annotation { "Feature Type Name" : "Feature", "Feature Type Description" : "" }
export const myFeature = defineFeature(function(context is Context, id is Id, definition is map)
    precondition{}
    {
        {
            var Q0;
            Q0=qCreatedBy(makeId("Front.planeOp"),FACE);
            var sketch = newSketch(context, id + "F0", { "sketchPlane" : qUnion([Q0])});
            skLineSegment(sketch, "E0.bottom", {"start": v(65, 37.5) * mm, "end": v(-65, 37.5) * mm});
            skLineSegment(sketch, "E0.top", {"start": v(65, -37.5) * mm, "end": v(-65, -37.5) * mm});
            skLineSegment(sketch, "E0.left", {"start": v(65, 37.5) * mm, "end": v(65, -37.5) * mm});
            skLineSegment(sketch, "E0.right", {"start": v(-65, 37.5) * mm, "end": v(-65, -37.5) * mm});
            skPoint(sketch, "E0.middle", {"position": v(0, 0) * mm});
            skSolve(sketch);
        }
        {
            var Q0;
            Q0 = qSketchRegion(id + "F0", true);
            extrude(context, id + "F1", {"entities" : qUnion([Q0]), "depth" : .6 * mm, "offsetDistance" : 25 * mm});
        }
        {
            var Q0;
            Q0=makeQuery(id+"F1.opExtrude","CAP_FACE",FACE,{"disambiguationData":[OSD([sQuery(id+"F0.wireOp",EDGE,"E0.bottom"),sQuery(id+"F0.wireOp",EDGE,"E0.top"),sQuery(id+"F0.wireOp",EDGE,"E0.left"),sQuery(id+"F0.wireOp",EDGE,"E0.right")])],"isStart":false});
            var sketch = newSketch(context, id + "F2", { "sketchPlane" : qUnion([Q0])});
            skText(sketch, "E1", { "text": "Prescription:", "fontName": "Tinos-Bold.ttf"});
            const initialGuessF2  = {"E1": [-0.064, 0.0285, 1, 0, 0.008]};
            skSetInitialGuess(sketch, initialGuessF2);
            skSolve(sketch);
        }
        {
            var Q0;
            Q0 = qSketchRegion(id + "F2", true);
            extrude(context, id + "F3", {"entities" : qUnion([Q0]), "operationType" : NewBodyOperationType.ADD, "depth" : .8 * mm, "offsetDistance" : 25 * mm});
        }
        {
            var Q0;
            {var subQ0=sQuery(id+"F0.wireOp",EDGE,"E0.bottom");var subQ1=sQuery(id+"F0.wireOp",EDGE,"E0.right");var subQ2=sQuery(id+"F0.wireOp",EDGE,"E0.top");var subQ3=sQuery(id+"F0.wireOp",EDGE,"E0.left");Q0=makeQuery(id+"F3.boolean.opBoolean","SPLIT",FACE,{"disambiguationData":[TD([makeQuery(id+"F1.opExtrude","SWEPT_FACE",FACE,{"disambiguationData":[OSD([subQ0])]})])],"derivedFrom":makeQuery(id+"F1.opExtrude","CAP_FACE",FACE,{"disambiguationData":[OSD([subQ0,subQ2,subQ3,subQ1])],"isStart":false})});}
            var sketch = newSketch(context, id + "F4", { "sketchPlane" : qUnion([Q0])});
            skText(sketch, "E2", { "text": "Beer", "fontName": "Tinos-Bold.ttf"});
            const initialGuessF4  = {"E2": [0.003, 0.0245, 1, 0, 0.01]};
            skSetInitialGuess(sketch, initialGuessF4);
            skSolve(sketch);
        }
        {
            var Q0;
            Q0 = qSketchRegion(id + "F4", true);
            extrude(context, id + "F5", {"entities" : qUnion([Q0]), "operationType" : NewBodyOperationType.ADD, "depth" : .8 * mm, "offsetDistance" : 25 * mm});
        }
        {
            var Q0;
            {var subQ118=sQuery(id+"F0.wireOp",EDGE,"E0.bottom");var subQ119=makeQuery(id+"F1.opExtrude","SWEPT_FACE",FACE,{"disambiguationData":[OSD([subQ118])]});var subQ124=sQuery(id+"F0.wireOp",EDGE,"E0.right");var subQ130=sQuery(id+"F0.wireOp",EDGE,"E0.top");var subQ139=sQuery(id+"F0.wireOp",EDGE,"E0.left");Q0=makeQuery(id+"F5.boolean.opBoolean","SPLIT",FACE,{"disambiguationData":[TD([subQ119])],"derivedFrom":makeQuery(id+"F3.boolean.opBoolean","SPLIT",FACE,{"disambiguationData":[TD([subQ119])],"derivedFrom":makeQuery(id+"F1.opExtrude","CAP_FACE",FACE,{"disambiguationData":[OSD([subQ118,subQ130,subQ139,subQ124])],"isStart":false})})});}
            var sketch = newSketch(context, id + "F6", { "sketchPlane" : qUnion([Q0])});
            skLineSegment(sketch, "E3.bottom", {"start": v(-65, 22.5) * mm, "end": v(65, 22.5) * mm});
            skLineSegment(sketch, "E3.top", {"start": v(-65, 21.5) * mm, "end": v(65, 21.5) * mm});
            skLineSegment(sketch, "E3.left", {"start": v(-65, 22.5) * mm, "end": v(-65, 21.5) * mm});
            skLineSegment(sketch, "E3.right", {"start": v(65, 22.5) * mm, "end": v(65, 21.5) * mm});
            skSolve(sketch);
        }
        {
            var Q0;
            Q0 = qSketchRegion(id + "F6", true);
            extrude(context, id + "F7", {"entities" : qUnion([Q0]), "operationType" : NewBodyOperationType.ADD, "depth" : .8 * mm, "offsetDistance" : 25 * mm});
        }
        {
            var Q0;
            {var subQ0=sQuery(id+"F0.wireOp",EDGE,"E0.right");var subQ2=sQuery(id+"F0.wireOp",EDGE,"E0.top");var subQ3=makeQuery(id+"F1.opExtrude","SWEPT_FACE",FACE,{"disambiguationData":[OSD([subQ2])]});var subQ4=sQuery(id+"F0.wireOp",EDGE,"E0.left");var subQ124=sQuery(id+"F0.wireOp",EDGE,"E0.bottom");var subQ125=makeQuery(id+"F1.opExtrude","SWEPT_FACE",FACE,{"disambiguationData":[OSD([subQ124])]});Q0=makeQuery(id+"F7.boolean.opBoolean","SPLIT",FACE,{"disambiguationData":[TD([subQ3])],"derivedFrom":makeQuery(id+"F5.boolean.opBoolean","SPLIT",FACE,{"disambiguationData":[TD([subQ125])],"derivedFrom":makeQuery(id+"F3.boolean.opBoolean","SPLIT",FACE,{"disambiguationData":[TD([subQ125])],"derivedFrom":makeQuery(id+"F1.opExtrude","CAP_FACE",FACE,{"disambiguationData":[OSD([subQ124,subQ2,subQ4,subQ0])],"isStart":false})})})});}
            var sketch = newSketch(context, id + "F8", { "sketchPlane" : qUnion([Q0])});
            skText(sketch, "E4", { "text": "Rx: #GET-HAPPY", "fontName": "OpenSans-Bold.ttf"});
            const initialGuessF8  = {"E4": [-0.063, 0.0115, 1, 0, 0.005]};
            skSetInitialGuess(sketch, initialGuessF8);
            skSolve(sketch);
        }
        {
            var Q0;
            Q0 = qSketchRegion(id + "F8", true);
            extrude(context, id + "F9", {"entities" : qUnion([Q0]), "operationType" : NewBodyOperationType.ADD, "depth" : .8 * mm, "offsetDistance" : 25 * mm});
        }
        {
            var Q0;
            {var subQ0=sQuery(id+"F0.wireOp",EDGE,"E0.right");var subQ2=sQuery(id+"F0.wireOp",EDGE,"E0.left");var subQ4=sQuery(id+"F0.wireOp",EDGE,"E0.top");var subQ5=makeQuery(id+"F1.opExtrude","SWEPT_FACE",FACE,{"disambiguationData":[OSD([subQ4])]});var subQ127=sQuery(id+"F0.wireOp",EDGE,"E0.bottom");var subQ128=makeQuery(id+"F1.opExtrude","SWEPT_FACE",FACE,{"disambiguationData":[OSD([subQ127])]});Q0=makeQuery(id+"F9.boolean.opBoolean","SPLIT",FACE,{"disambiguationData":[TD([subQ5])],"derivedFrom":makeQuery(id+"F7.boolean.opBoolean","SPLIT",FACE,{"disambiguationData":[TD([subQ5])],"derivedFrom":makeQuery(id+"F5.boolean.opBoolean","SPLIT",FACE,{"disambiguationData":[TD([subQ128])],"derivedFrom":makeQuery(id+"F3.boolean.opBoolean","SPLIT",FACE,{"disambiguationData":[TD([subQ128])],"derivedFrom":makeQuery(id+"F1.opExtrude","CAP_FACE",FACE,{"disambiguationData":[OSD([subQ127,subQ4,subQ2,subQ0])],"isStart":false})})})})});}
            var sketch = newSketch(context, id + "F10", { "sketchPlane" : qUnion([Q0])});
            skText(sketch, "E5", { "text": "Doctor: Harold Hopps", "fontName": "Tinos-Bold.ttf"});
            const initialGuessF10  = {"E5": [-0.063, 0.006, 1, 0, 0.006]};
            skSetInitialGuess(sketch, initialGuessF10);
            skSolve(sketch);
        }
        {
            var Q0;
            Q0 = qSketchRegion(id + "F10", true);
            extrude(context, id + "F11", {"entities" : qUnion([Q0]), "operationType" : NewBodyOperationType.ADD, "depth" : .8 * mm, "offsetDistance" : 25 * mm});
        }
        {
            var Q0;
            {var subQ40=sQuery(id+"F0.wireOp",EDGE,"E0.right");var subQ43=sQuery(id+"F0.wireOp",EDGE,"E0.left");var subQ46=sQuery(id+"F0.wireOp",EDGE,"E0.top");var subQ47=makeQuery(id+"F1.opExtrude","SWEPT_FACE",FACE,{"disambiguationData":[OSD([subQ46])]});var subQ285=sQuery(id+"F0.wireOp",EDGE,"E0.bottom");var subQ286=makeQuery(id+"F1.opExtrude","SWEPT_FACE",FACE,{"disambiguationData":[OSD([subQ285])]});Q0=makeQuery(id+"F11.boolean.opBoolean","SPLIT",FACE,{"disambiguationData":[TD([subQ47])],"derivedFrom":makeQuery(id+"F9.boolean.opBoolean","SPLIT",FACE,{"disambiguationData":[TD([subQ47])],"derivedFrom":makeQuery(id+"F7.boolean.opBoolean","SPLIT",FACE,{"disambiguationData":[TD([subQ47])],"derivedFrom":makeQuery(id+"F5.boolean.opBoolean","SPLIT",FACE,{"disambiguationData":[TD([subQ286])],"derivedFrom":makeQuery(id+"F3.boolean.opBoolean","SPLIT",FACE,{"disambiguationData":[TD([subQ286])],"derivedFrom":makeQuery(id+"F1.opExtrude","CAP_FACE",FACE,{"disambiguationData":[OSD([subQ285,subQ46,subQ43,subQ40])],"isStart":false})})})})})});}
            var sketch = newSketch(context, id + "F12", { "sketchPlane" : qUnion([Q0])});
            skText(sketch, "E6", { "text": "Refills: Absolutely", "fontName": "Tinos-Bold.ttf"});
            const initialGuessF12  = {"E6": [-0.063, -0.0355, 1, 0, 0.006]};
            skSetInitialGuess(sketch, initialGuessF12);
            skSolve(sketch);
        }
        {
            var Q0;
            Q0 = qSketchRegion(id + "F12", true);
            extrude(context, id + "F13", {"entities" : qUnion([Q0]), "operationType" : NewBodyOperationType.ADD, "depth" : 1 * mm, "offsetDistance" : 25 * mm});
        }
        {
            var Q0;
            {var subQ159=sQuery(id+"F0.wireOp",EDGE,"E0.right");var subQ163=sQuery(id+"F0.wireOp",EDGE,"E0.left");var subQ167=sQuery(id+"F0.wireOp",EDGE,"E0.top");var subQ168=makeQuery(id+"F1.opExtrude","SWEPT_FACE",FACE,{"disambiguationData":[OSD([subQ167])]});var subQ592=sQuery(id+"F0.wireOp",EDGE,"E0.bottom");var subQ593=makeQuery(id+"F1.opExtrude","SWEPT_FACE",FACE,{"disambiguationData":[OSD([subQ592])]});Q0=makeQuery(id+"F13.boolean.opBoolean","SPLIT",FACE,{"disambiguationData":[TD([subQ168])],"derivedFrom":makeQuery(id+"F11.boolean.opBoolean","SPLIT",FACE,{"disambiguationData":[TD([subQ168])],"derivedFrom":makeQuery(id+"F9.boolean.opBoolean","SPLIT",FACE,{"disambiguationData":[TD([subQ168])],"derivedFrom":makeQuery(id+"F7.boolean.opBoolean","SPLIT",FACE,{"disambiguationData":[TD([subQ168])],"derivedFrom":makeQuery(id+"F5.boolean.opBoolean","SPLIT",FACE,{"disambiguationData":[TD([subQ593])],"derivedFrom":makeQuery(id+"F3.boolean.opBoolean","SPLIT",FACE,{"disambiguationData":[TD([subQ593])],"derivedFrom":makeQuery(id+"F1.opExtrude","CAP_FACE",FACE,{"disambiguationData":[OSD([subQ592,subQ167,subQ163,subQ159])],"isStart":false})})})})})})});}
            var sketch = newSketch(context, id + "F14", { "sketchPlane" : qUnion([Q0])});
            skText(sketch, "E7", { "text": "Expires: Never!", "fontName": "Tinos-Bold.ttf"});
            const initialGuessF14  = {"E7": [0.00696, -0.0355, 1, 0, 0.006]};
            skSetInitialGuess(sketch, initialGuessF14);
            skSolve(sketch);
        }
        {
            var Q0;
            Q0 = qSketchRegion(id + "F14", true);
            extrude(context, id + "F15", {"entities" : qUnion([Q0]), "operationType" : NewBodyOperationType.ADD, "depth" : .8 * mm, "offsetDistance" : 25 * mm});
        }
        {
            var Q0;
            {var subQ548=sQuery(id+"F0.wireOp",EDGE,"E0.top");var subQ549=makeQuery(id+"F1.opExtrude","SWEPT_FACE",FACE,{"disambiguationData":[OSD([subQ548])]});var subQ553=sQuery(id+"F0.wireOp",EDGE,"E0.left");var subQ557=sQuery(id+"F0.wireOp",EDGE,"E0.right");var subQ900=sQuery(id+"F0.wireOp",EDGE,"E0.bottom");var subQ901=makeQuery(id+"F1.opExtrude","SWEPT_FACE",FACE,{"disambiguationData":[OSD([subQ900])]});Q0=makeQuery(id+"F15.boolean.opBoolean","SPLIT",FACE,{"disambiguationData":[TD([subQ549])],"derivedFrom":makeQuery(id+"F13.boolean.opBoolean","SPLIT",FACE,{"disambiguationData":[TD([subQ549])],"derivedFrom":makeQuery(id+"F11.boolean.opBoolean","SPLIT",FACE,{"disambiguationData":[TD([subQ549])],"derivedFrom":makeQuery(id+"F9.boolean.opBoolean","SPLIT",FACE,{"disambiguationData":[TD([subQ549])],"derivedFrom":makeQuery(id+"F7.boolean.opBoolean","SPLIT",FACE,{"disambiguationData":[TD([subQ549])],"derivedFrom":makeQuery(id+"F5.boolean.opBoolean","SPLIT",FACE,{"disambiguationData":[TD([subQ901])],"derivedFrom":makeQuery(id+"F3.boolean.opBoolean","SPLIT",FACE,{"disambiguationData":[TD([subQ901])],"derivedFrom":makeQuery(id+"F1.opExtrude","CAP_FACE",FACE,{"disambiguationData":[OSD([subQ900,subQ548,subQ553,subQ557])],"isStart":false})})})})})})})});}
            var sketch = newSketch(context, id + "F16", { "sketchPlane" : qUnion([Q0])});
            skText(sketch, "E8", { "text": "R. Stevenson: Take as desired", "fontName": "Tinos-Bold.ttf"});
            const initialGuessF16  = {"E8": [-0.063, -0.0035, 1, 0, 0.007]};
            skSetInitialGuess(sketch, initialGuessF16);
            skSolve(sketch);
        }
        {
            var Q0;
            Q0 = qSketchRegion(id + "F16", true);
            extrude(context, id + "F17", {"entities" : qUnion([Q0]), "operationType" : NewBodyOperationType.ADD, "depth" : 1 * mm, "offsetDistance" : 25 * mm});
        }
        {
            var Q0;
            {var subQ593=sQuery(id+"F0.wireOp",EDGE,"E0.top");var subQ594=makeQuery(id+"F1.opExtrude","SWEPT_FACE",FACE,{"disambiguationData":[OSD([subQ593])]});var subQ598=sQuery(id+"F0.wireOp",EDGE,"E0.left");var subQ602=sQuery(id+"F0.wireOp",EDGE,"E0.right");var subQ1162=sQuery(id+"F0.wireOp",EDGE,"E0.bottom");var subQ1163=makeQuery(id+"F1.opExtrude","SWEPT_FACE",FACE,{"disambiguationData":[OSD([subQ1162])]});Q0=makeQuery(id+"F17.boolean.opBoolean","SPLIT",FACE,{"disambiguationData":[TD([subQ594])],"derivedFrom":makeQuery(id+"F15.boolean.opBoolean","SPLIT",FACE,{"disambiguationData":[TD([subQ594])],"derivedFrom":makeQuery(id+"F13.boolean.opBoolean","SPLIT",FACE,{"disambiguationData":[TD([subQ594])],"derivedFrom":makeQuery(id+"F11.boolean.opBoolean","SPLIT",FACE,{"disambiguationData":[TD([subQ594])],"derivedFrom":makeQuery(id+"F9.boolean.opBoolean","SPLIT",FACE,{"disambiguationData":[TD([subQ594])],"derivedFrom":makeQuery(id+"F7.boolean.opBoolean","SPLIT",FACE,{"disambiguationData":[TD([subQ594])],"derivedFrom":makeQuery(id+"F5.boolean.opBoolean","SPLIT",FACE,{"disambiguationData":[TD([subQ1163])],"derivedFrom":makeQuery(id+"F3.boolean.opBoolean","SPLIT",FACE,{"disambiguationData":[TD([subQ1163])],"derivedFrom":makeQuery(id+"F1.opExtrude","CAP_FACE",FACE,{"disambiguationData":[OSD([subQ1162,subQ593,subQ598,subQ602])],"isStart":false})})})})})})})})});}
            var sketch = newSketch(context, id + "F18", { "sketchPlane" : qUnion([Q0])});
            skText(sketch, "E9", { "text": "Contains: Liquid Happiness \nand sunshine 473 ml, dose.", "fontName": "Tinos-Bold.ttf"});
            const initialGuessF18  = {"E9": [-0.063, -0.0155, 1, 0, 0.007]};
            skSetInitialGuess(sketch, initialGuessF18);
            skSolve(sketch);
        }
        {
            var Q0;
            Q0 = qSketchRegion(id + "F18", true);
            extrude(context, id + "F19", {"entities" : qUnion([Q0]), "operationType" : NewBodyOperationType.ADD, "depth" : .8 * mm, "offsetDistance" : 25 * mm});
        }
        {
            var Q0;
            Q0=makeQuery(id+"F7.opExtrude","CAP_EDGE",EDGE,{"disambiguationData":[OSD([sQuery(id+"F6.wireOp",EDGE,"E3.bottom")])],"isStart":true});
            var Q1;
            Q1=makeQuery(id+"F7.opExtrude","CAP_EDGE",EDGE,{"disambiguationData":[OSD([sQuery(id+"F6.wireOp",EDGE,"E3.top")])],"isStart":true});
            fillet(context, id + "F20", {"entities" : qUnion([Q0, Q1]), "radius" : .5 * mm, "tangentPropagation" : true, "allowEdgeOverflow" : false});
        }
        {
            var Q0;
            Q0=makeQuery(id+"F1.opExtrude","SWEPT_EDGE",EDGE,{"disambiguationData":[OSD([sQuery(id+"F0.wireOp",EDGE,"E0.top"),sQuery(id+"F0.wireOp",EDGE,"E0.right")])]});
            var Q1;
            Q1=makeQuery(id+"F1.opExtrude","SWEPT_EDGE",EDGE,{"disambiguationData":[OSD([sQuery(id+"F0.wireOp",EDGE,"E0.bottom"),sQuery(id+"F0.wireOp",EDGE,"E0.right")])]});
            var Q2;
            Q2=makeQuery(id+"F1.opExtrude","SWEPT_EDGE",EDGE,{"disambiguationData":[OSD([sQuery(id+"F0.wireOp",EDGE,"E0.bottom"),sQuery(id+"F0.wireOp",EDGE,"E0.left")])]});
            var Q3;
            Q3=makeQuery(id+"F1.opExtrude","SWEPT_EDGE",EDGE,{"disambiguationData":[OSD([sQuery(id+"F0.wireOp",EDGE,"E0.top"),sQuery(id+"F0.wireOp",EDGE,"E0.left")])]});
            fillet(context, id + "F21", {"entities" : qUnion([Q0, Q1, Q2, Q3]), "radius" : 2 * mm, "tangentPropagation" : true, "allowEdgeOverflow" : false});
        }
    });